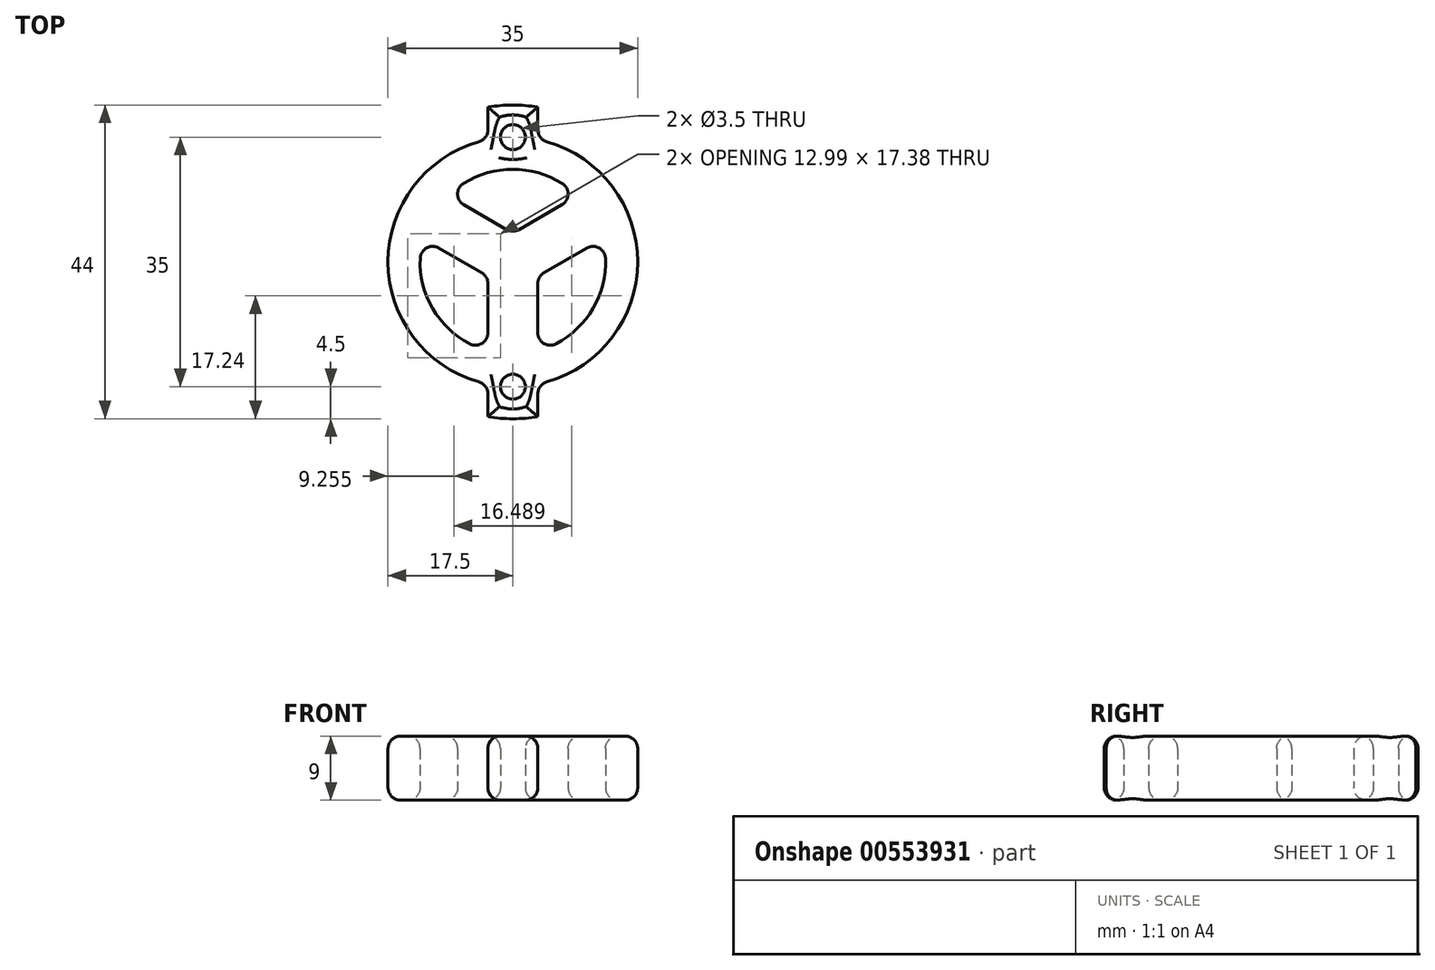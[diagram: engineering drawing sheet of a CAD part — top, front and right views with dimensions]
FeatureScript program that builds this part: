
annotation { "Feature Type Name" : "Feature", "Feature Type Description" : "" }
export const myFeature = defineFeature(function(context is Context, id is Id, definition is map)
    precondition{}
    {
        {
            var Q0;
            Q0=qCreatedBy(makeId("Top.planeOp"),FACE);
            var sketch = newSketch(context, id + "F0", { "sketchPlane" : qUnion([Q0])});
            skLineSegment(sketch, "E0", {"start": v(0, 60) * mm, "end": v(0, -60) * mm});
            skLineSegment(sketch, "E1", {"start": v(-70, 0) * mm, "end": v(70, 0) * mm});
            skArc(sketch, "E2", {"start": v(-3.5, 17.15) * mm, "mid": v(-17.5, 0) * mm, "end": v(-3.5, -17.15) * mm});
            skArc(sketch, "E3", {"start": v(-12.6, 3.23) * mm, "mid": v(-11.26, -6.5) * mm, "end": v(-3.5, -12.52) * mm});
            skLineSegment(sketch, "E4", {"start": v(3.5, 21.72) * mm, "end": v(3.5, 17.15) * mm});
            skLineSegment(sketch, "E5", {"start": v(-3.5, 21.72) * mm, "end": v(-3.5, 17.15) * mm});
            skLineSegment(sketch, "E6", {"start": v(0, 4.04) * mm, "end": v(-9.1, 9.3) * mm});
            skLineSegment(sketch, "E7", {"start": v(-3.5, -2.02) * mm, "end": v(-12.6, 3.23) * mm});
            skLineSegment(sketch, "E8", {"start": v(0, 4.04) * mm, "end": v(9.1, 9.3) * mm});
            skLineSegment(sketch, "E9", {"start": v(3.5, -2.02) * mm, "end": v(12.6, 3.23) * mm});
            skArc(sketch, "E10", {"start": v(3.5, -12.52) * mm, "mid": v(11.26, -6.5) * mm, "end": v(12.6, 3.23) * mm});
            skArc(sketch, "E11", {"start": v(9.1, 9.3) * mm, "mid": v(0, 13) * mm, "end": v(-9.1, 9.3) * mm});
            skArc(sketch, "E12", {"start": v(-3.5, -21.72) * mm, "mid": v(0, -22) * mm, "end": v(3.5, -21.72) * mm});
            skArc(sketch, "E13", {"start": v(3.5, 21.72) * mm, "mid": v(0, 22) * mm, "end": v(-3.5, 21.72) * mm});
            skArc(sketch, "E14", {"start": v(3.5, -17.15) * mm, "mid": v(17.5, 0) * mm, "end": v(3.5, 17.15) * mm});
            skLineSegment(sketch, "E15", {"start": v(-3.5, -17.15) * mm, "end": v(-3.5, -21.72) * mm});
            skLineSegment(sketch, "E16", {"start": v(3.5, -17.15) * mm, "end": v(3.5, -21.72) * mm});
            skLineSegment(sketch, "E17", {"start": v(-3.5, -2.02) * mm, "end": v(-3.5, -12.52) * mm});
            skLineSegment(sketch, "E18", {"start": v(3.5, -2.02) * mm, "end": v(3.5, -12.52) * mm});
            skCircle(sketch, "E19", {"center": v(0, 17.5) * mm, "radius": 1.75 * mm});
            skCircle(sketch, "E20", {"center": v(0, -17.5) * mm, "radius": 1.75 * mm});
            skSolve(sketch);
        }
        {
            var Q0;
            {var subQ16=sQuery(id+"F0.wireOp",EDGE,"E4");Q0=makeQuery(id+"F0.imprint","IMPRINT",FACE,{"disambiguationData":[TD([[makeQuery(id+"F0.imprint","IMPRINT",EDGE,{"derivedFrom":subQ16}),-1.0]])]});}
            var Q1;
            {var subQ1=sQuery(id+"F0.wireOp",EDGE,"E16");Q1=makeQuery(id+"F0.imprint","IMPRINT",FACE,{"disambiguationData":[TD([[makeQuery(id+"F0.imprint","IMPRINT",EDGE,{"derivedFrom":subQ1}),-1.0]])]});}
            var Q2;
            {var subQ0=sQuery(id+"F0.wireOp",EDGE,"E15");Q2=makeQuery(id+"F0.imprint","IMPRINT",FACE,{"disambiguationData":[TD([[makeQuery(id+"F0.imprint","IMPRINT",EDGE,{"derivedFrom":subQ0}),1.0]])]});}
            var Q3;
            {var subQ6=sQuery(id+"F0.wireOp",EDGE,"E5");Q3=makeQuery(id+"F0.imprint","IMPRINT",FACE,{"disambiguationData":[TD([[makeQuery(id+"F0.imprint","IMPRINT",EDGE,{"derivedFrom":subQ6}),1.0]])]});}
            extrude(context, id + "F1", {"entities" : qUnion([Q0, Q1, Q2, Q3]), "depth" : 9 * mm, "offsetDistance" : 25 * mm});
        }
        {
            var Q0;
            Q0=makeQuery(id+"F1.opExtrude","SWEPT_EDGE",EDGE,{"disambiguationData":[OSD([sQuery(id+"F0.wireOp",EDGE,"E3"),sQuery(id+"F0.wireOp",EDGE,"E7")])]});
            var Q1;
            Q1=makeQuery(id+"F1.opExtrude","SWEPT_EDGE",EDGE,{"disambiguationData":[OSD([sQuery(id+"F0.wireOp",EDGE,"E14"),sQuery(id+"F0.wireOp",EDGE,"E16")])]});
            var Q2;
            Q2=makeQuery(id+"F1.opExtrude","SWEPT_EDGE",EDGE,{"disambiguationData":[OSD([sQuery(id+"F0.wireOp",EDGE,"E2"),sQuery(id+"F0.wireOp",EDGE,"E15")])]});
            var Q3;
            Q3=makeQuery(id+"F1.opExtrude","SWEPT_EDGE",EDGE,{"disambiguationData":[OSD([sQuery(id+"F0.wireOp",EDGE,"E7"),sQuery(id+"F0.wireOp",EDGE,"E17")])]});
            var Q4;
            Q4=makeQuery(id+"F1.opExtrude","SWEPT_EDGE",EDGE,{"disambiguationData":[OSD([sQuery(id+"F0.wireOp",EDGE,"E9"),sQuery(id+"F0.wireOp",EDGE,"E10")])]});
            var Q5;
            Q5=makeQuery(id+"F1.opExtrude","SWEPT_EDGE",EDGE,{"disambiguationData":[OSD([sQuery(id+"F0.wireOp",EDGE,"E2"),sQuery(id+"F0.wireOp",EDGE,"E5")])]});
            var Q6;
            Q6=makeQuery(id+"F1.opExtrude","SWEPT_EDGE",EDGE,{"disambiguationData":[OSD([sQuery(id+"F0.wireOp",EDGE,"E0"),sQuery(id+"F0.wireOp",EDGE,"E6"),sQuery(id+"F0.wireOp",EDGE,"E8")])]});
            var Q7;
            Q7=makeQuery(id+"F1.opExtrude","SWEPT_EDGE",EDGE,{"disambiguationData":[OSD([sQuery(id+"F0.wireOp",EDGE,"E4"),sQuery(id+"F0.wireOp",EDGE,"E14")])]});
            var Q8;
            Q8=makeQuery(id+"F1.opExtrude","SWEPT_EDGE",EDGE,{"disambiguationData":[OSD([sQuery(id+"F0.wireOp",EDGE,"E9"),sQuery(id+"F0.wireOp",EDGE,"E18")])]});
            var Q9;
            Q9=makeQuery(id+"F1.opExtrude","SWEPT_EDGE",EDGE,{"disambiguationData":[OSD([sQuery(id+"F0.wireOp",EDGE,"E6"),sQuery(id+"F0.wireOp",EDGE,"E11")])]});
            var Q10;
            Q10=makeQuery(id+"F1.opExtrude","SWEPT_EDGE",EDGE,{"disambiguationData":[OSD([sQuery(id+"F0.wireOp",EDGE,"E3"),sQuery(id+"F0.wireOp",EDGE,"E17")])]});
            var Q11;
            Q11=makeQuery(id+"F1.opExtrude","SWEPT_EDGE",EDGE,{"disambiguationData":[OSD([sQuery(id+"F0.wireOp",EDGE,"E10"),sQuery(id+"F0.wireOp",EDGE,"E18")])]});
            var Q12;
            Q12=makeQuery(id+"F1.opExtrude","SWEPT_EDGE",EDGE,{"disambiguationData":[OSD([sQuery(id+"F0.wireOp",EDGE,"E8"),sQuery(id+"F0.wireOp",EDGE,"E11")])]});
            var Q13;
            Q13=makeQuery(id+"F1.opExtrude","CAP_EDGE",EDGE,{"disambiguationData":[OSD([sQuery(id+"F0.wireOp",EDGE,"E7")])],"isStart":false});
            var Q14;
            Q14=makeQuery(id+"F1.opExtrude","CAP_EDGE",EDGE,{"disambiguationData":[OSD([sQuery(id+"F0.wireOp",EDGE,"E9")])],"isStart":false});
            var Q15;
            Q15=makeQuery(id+"F1.opExtrude","CAP_FACE",FACE,{"disambiguationData":[OSD([sQuery(id+"F0.wireOp",EDGE,"E2"),sQuery(id+"F0.wireOp",EDGE,"E3"),sQuery(id+"F0.wireOp",EDGE,"E4"),sQuery(id+"F0.wireOp",EDGE,"E5"),sQuery(id+"F0.wireOp",EDGE,"E6"),sQuery(id+"F0.wireOp",EDGE,"E7"),sQuery(id+"F0.wireOp",EDGE,"E8"),sQuery(id+"F0.wireOp",EDGE,"E9"),sQuery(id+"F0.wireOp",EDGE,"E10"),sQuery(id+"F0.wireOp",EDGE,"E11"),sQuery(id+"F0.wireOp",EDGE,"E12"),sQuery(id+"F0.wireOp",EDGE,"E13"),sQuery(id+"F0.wireOp",EDGE,"E14"),sQuery(id+"F0.wireOp",EDGE,"E15"),sQuery(id+"F0.wireOp",EDGE,"E16"),sQuery(id+"F0.wireOp",EDGE,"E17"),sQuery(id+"F0.wireOp",EDGE,"E18"),sQuery(id+"F0.wireOp",EDGE,"E19"),sQuery(id+"F0.wireOp",EDGE,"E20")])],"isStart":false});
            var Q16;
            Q16=makeQuery(id+"F1.opExtrude","CAP_FACE",FACE,{"disambiguationData":[OSD([sQuery(id+"F0.wireOp",EDGE,"E2"),sQuery(id+"F0.wireOp",EDGE,"E3"),sQuery(id+"F0.wireOp",EDGE,"E4"),sQuery(id+"F0.wireOp",EDGE,"E5"),sQuery(id+"F0.wireOp",EDGE,"E6"),sQuery(id+"F0.wireOp",EDGE,"E7"),sQuery(id+"F0.wireOp",EDGE,"E8"),sQuery(id+"F0.wireOp",EDGE,"E9"),sQuery(id+"F0.wireOp",EDGE,"E10"),sQuery(id+"F0.wireOp",EDGE,"E11"),sQuery(id+"F0.wireOp",EDGE,"E12"),sQuery(id+"F0.wireOp",EDGE,"E13"),sQuery(id+"F0.wireOp",EDGE,"E14"),sQuery(id+"F0.wireOp",EDGE,"E15"),sQuery(id+"F0.wireOp",EDGE,"E16"),sQuery(id+"F0.wireOp",EDGE,"E17"),sQuery(id+"F0.wireOp",EDGE,"E18"),sQuery(id+"F0.wireOp",EDGE,"E19"),sQuery(id+"F0.wireOp",EDGE,"E20")])],"isStart":true});
            fillet(context, id + "F2", {"entities" : qUnion([Q0, Q1, Q2, Q3, Q4, Q5, Q6, Q7, Q8, Q9, Q10, Q11, Q12, Q13, Q14, Q15, Q16]), "radius" : (3.5 / 2) * mm, "tangentPropagation" : true, "allowEdgeOverflow" : false});
        }
    });
